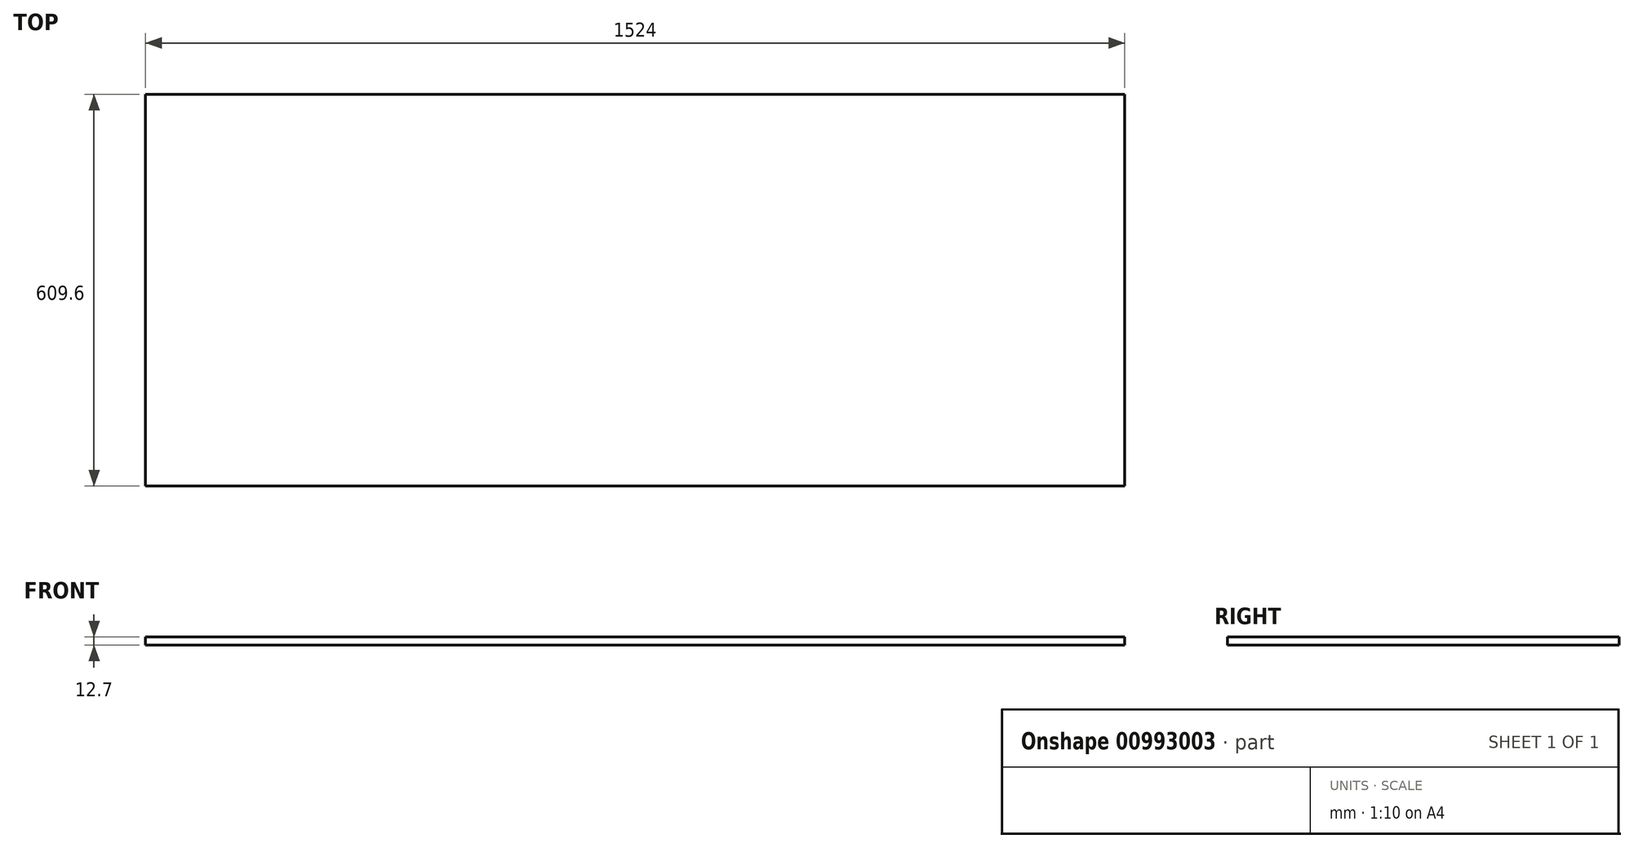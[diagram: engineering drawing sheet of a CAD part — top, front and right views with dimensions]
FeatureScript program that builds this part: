
annotation { "Feature Type Name" : "Feature", "Feature Type Description" : "" }
export const myFeature = defineFeature(function(context is Context, id is Id, definition is map)
    precondition{}
    {
        {
            var Q0;
            Q0=qCreatedBy(makeId("Top.planeOp"),FACE);
            var sketch = newSketch(context, id + "F0", { "sketchPlane" : qUnion([Q0])});
            skLineSegment(sketch, "E0", {"start": v(0, 0) * mm, "end": v(1524, 0) * mm});
            skLineSegment(sketch, "E1", {"start": v(0, 0) * mm, "end": v(0, 609.6) * mm});
            skLineSegment(sketch, "E2", {"start": v(0, 609.6) * mm, "end": v(1524, 609.6) * mm});
            skLineSegment(sketch, "E3", {"start": v(1524, 609.6) * mm, "end": v(1524, 0) * mm});
            skSolve(sketch);
        }
        {
            var Q0;
            Q0=makeQuery(id+"F0.imprint","IMPRINT",FACE,{"disambiguationData":[TD([[makeQuery(id+"F0.imprint","IMPRINT",EDGE,{"derivedFrom":sQuery(id+"F0.wireOp",EDGE,"E0")}),1.0]])]});
            extrude(context, id + "F1", {"entities" : qUnion([Q0]), "depth" : 12.7 * mm, "offsetDistance" : 25.4 * mm});
        }
    });
